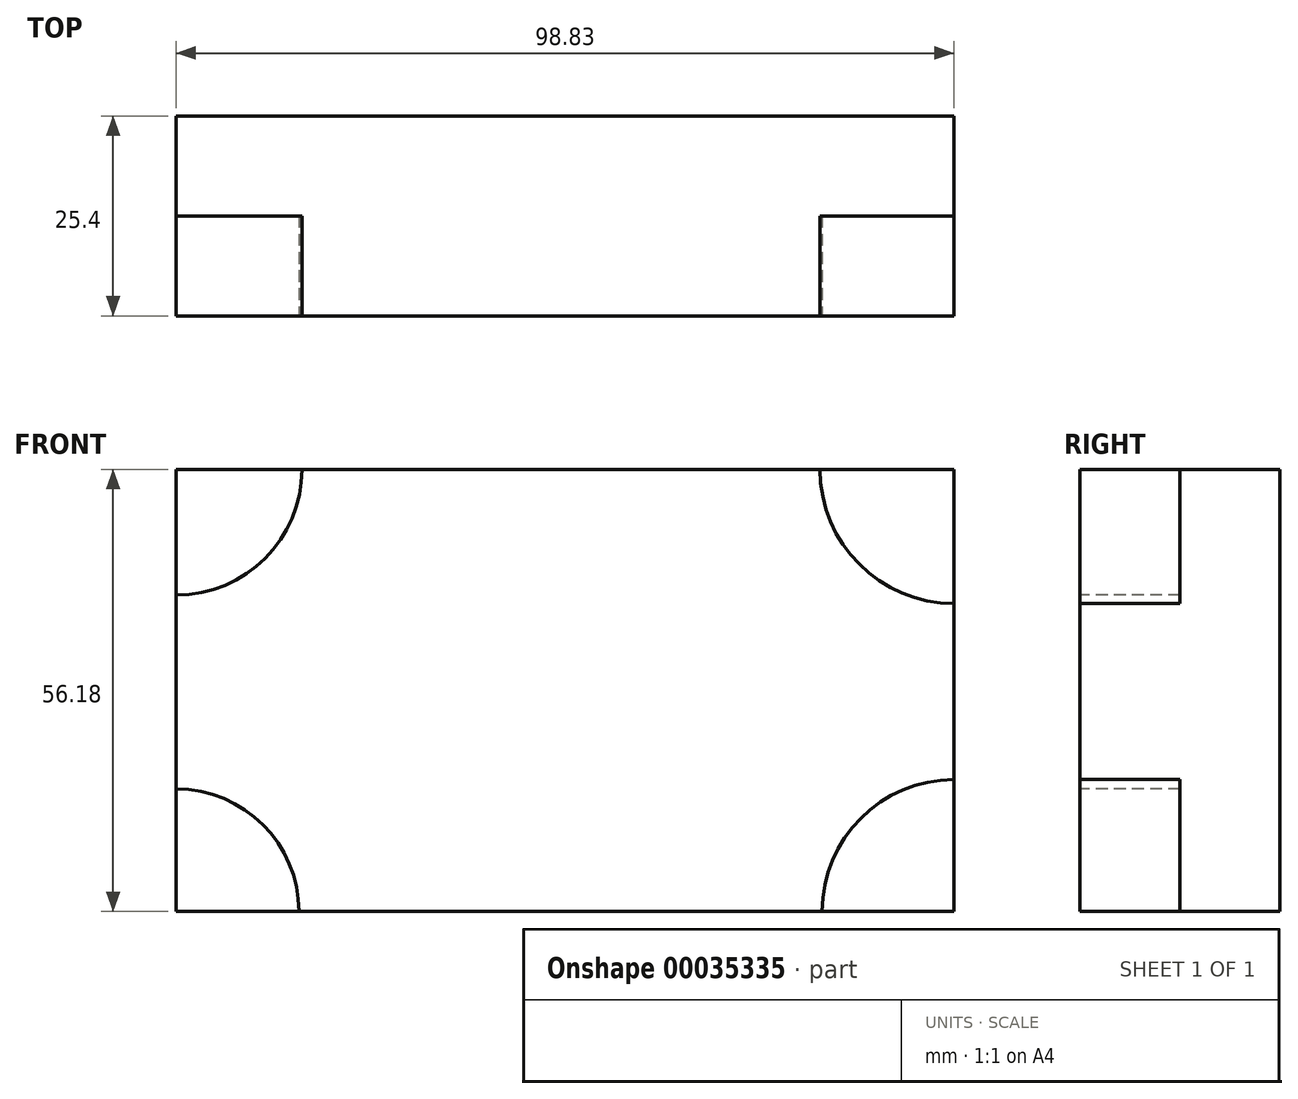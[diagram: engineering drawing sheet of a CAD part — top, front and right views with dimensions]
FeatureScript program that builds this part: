
annotation { "Feature Type Name" : "Feature", "Feature Type Description" : "" }
export const myFeature = defineFeature(function(context is Context, id is Id, definition is map)
    precondition{}
    {
        {
            var Q0;
            Q0=qCreatedBy(makeId("Front.planeOp"),FACE);
            var sketch = newSketch(context, id + "F0", { "sketchPlane" : qUnion([Q0])});
            skLineSegment(sketch, "E0.bottom", {"start": v(-48.2, 21.77) * mm, "end": v(50.62, 21.77) * mm});
            skLineSegment(sketch, "E0.top", {"start": v(-48.2, -34.41) * mm, "end": v(50.62, -34.41) * mm});
            skLineSegment(sketch, "E0.left", {"start": v(-48.2, 21.77) * mm, "end": v(-48.2, -34.41) * mm});
            skLineSegment(sketch, "E0.right", {"start": v(50.62, 21.77) * mm, "end": v(50.62, -34.41) * mm});
            skSolve(sketch);
        }
        {
            var Q0;
            Q0 = qSketchRegion(id + "F0", true);
            extrude(context, id + "F1", {"entities" : qUnion([Q0]), "depth" : 25.4 * mm});
        }
        {
            var Q0;
            Q0=makeQuery(id+"F1.opExtrude","CAP_FACE",FACE,{"disambiguationData":[OSD([sQuery(id+"F0.wireOp",EDGE,"E0.bottom"),sQuery(id+"F0.wireOp",EDGE,"E0.top"),sQuery(id+"F0.wireOp",EDGE,"E0.left"),sQuery(id+"F0.wireOp",EDGE,"E0.right")])],"isStart":false});
            var sketch = newSketch(context, id + "F2", { "sketchPlane" : qUnion([Q0])});
            skCircle(sketch, "E1", {"center": v(50.62, 21.77) * mm, "radius": 17.03 * mm});
            skCircle(sketch, "E2", {"center": v(-48.2, 21.77) * mm, "radius": 15.98 * mm});
            skCircle(sketch, "E3", {"center": v(-48.2, -34.41) * mm, "radius": 15.6 * mm});
            skCircle(sketch, "E4", {"center": v(50.62, -34.41) * mm, "radius": 16.77 * mm});
            skSolve(sketch);
        }
        {
            var Q0;
            Q0 = qSketchRegion(id + "F2", true);
            extrude(context, id + "F3", {"entities" : qUnion([Q0]), "operationType" : NewBodyOperationType.REMOVE, "oppositeDirection" : true, "depth" : 12.7 * mm});
        }
    });
